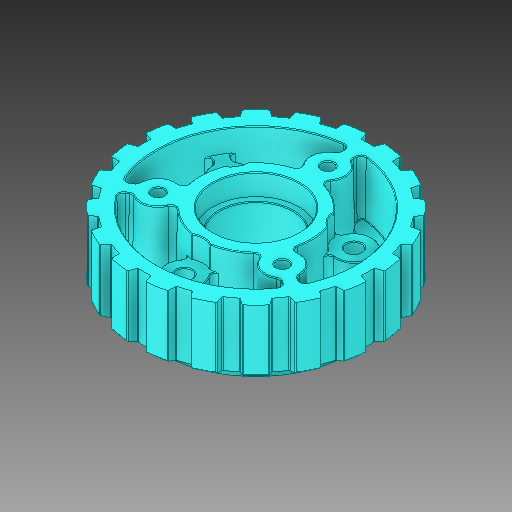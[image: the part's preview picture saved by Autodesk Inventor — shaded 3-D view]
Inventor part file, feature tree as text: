
AUTODESK INVENTOR PART (.ipt)
format: ipt  version: 2019 (Build 230136000, 136)  size: 1,392,640 bytes
history: native  units: in
note: dims shown in document units (in); Inventor stores cm internally (conversion verified against a paired STEP export)
features: fillet x1
ambient origin geometry x8: Origin, YZ Plane, XZ Plane, XY Plane, X Axis, Y Axis, Z Axis, Center Point
bodies: Solid1 (feature_tree)
feature tree (1):
  fillet  "Fillet4"  [1 undecoded]
note: 1 required parameter value undecoded (feature->parameter linkage not recoverable at this tier; creation-order binding heuristic only, values carry confidence <= 0.55)
